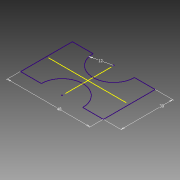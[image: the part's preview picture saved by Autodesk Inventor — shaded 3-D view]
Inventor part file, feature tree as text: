
AUTODESK INVENTOR PART (.ipt)
format: ipt  version: 2015 (Build 190159000, 159)  size: 70,144 bytes
history: native  units: mm
features: sketch x1
ambient origin geometry x8: Origin, YZ Plane, XZ Plane, XY Plane, X Axis, Y Axis, Z Axis, Center Point
feature tree (1):
  sketch  "Sketch1"  dims[d0=30.0mm d1=48.0mm d2=12.0mm]
